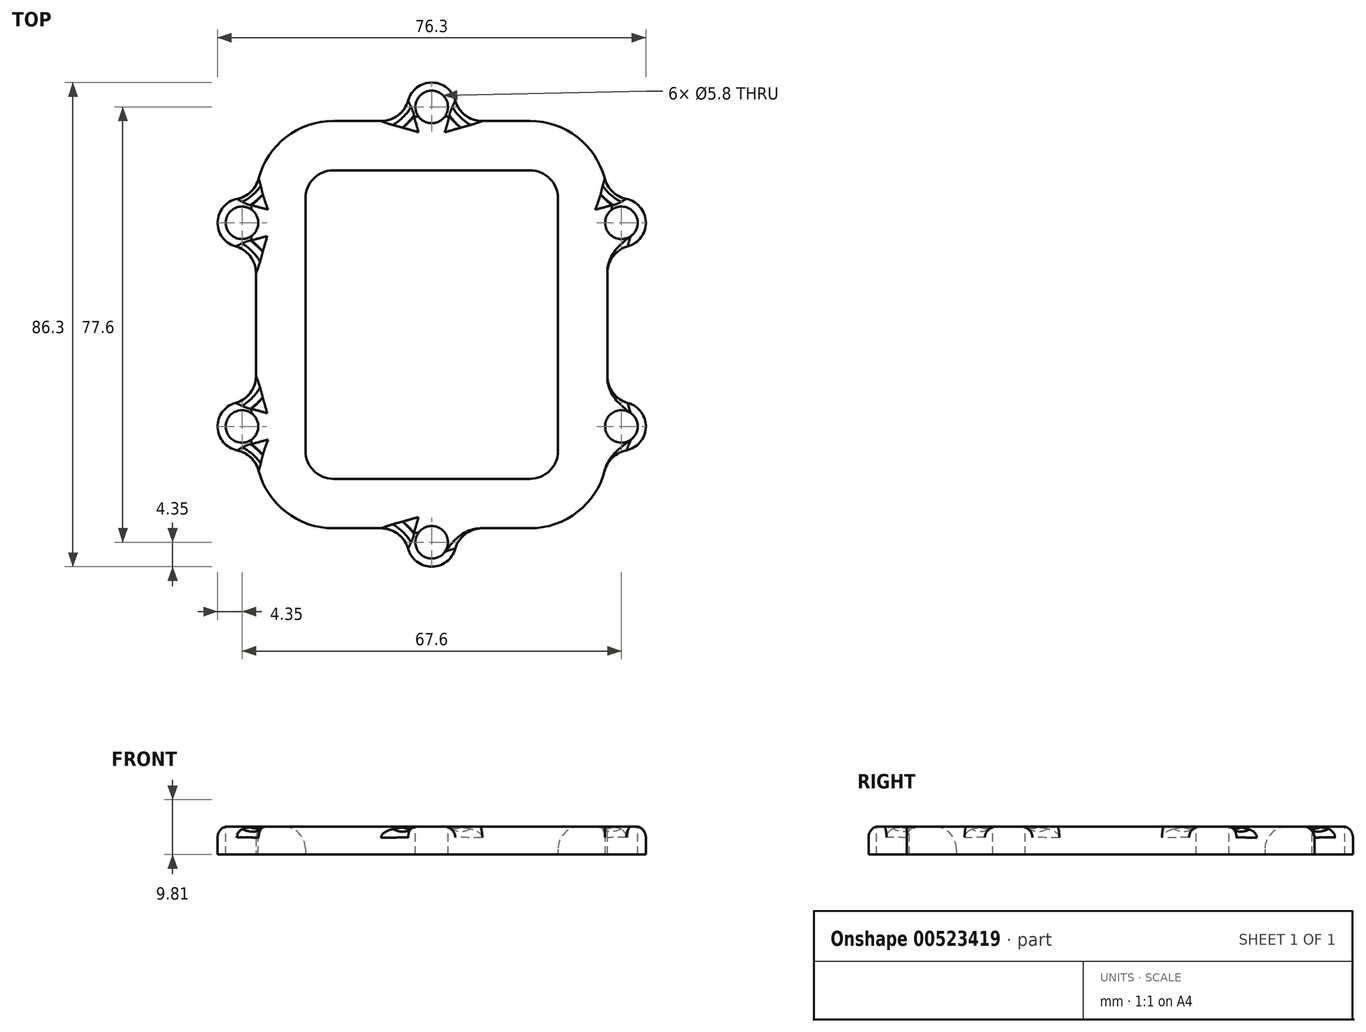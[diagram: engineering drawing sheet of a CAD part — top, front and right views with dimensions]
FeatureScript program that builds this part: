
annotation { "Feature Type Name" : "Feature", "Feature Type Description" : "" }
export const myFeature = defineFeature(function(context is Context, id is Id, definition is map)
    precondition{}
    {
        {
            var Q0;
            Q0=qCreatedBy(makeId("Top.planeOp"),FACE);
            var sketch = newSketch(context, id + "F0", { "sketchPlane" : qUnion([Q0])});
            skLineSegment(sketch, "E0.bottom", {"start": v(-17.5, -27.5) * mm, "end": v(17.5, -27.5) * mm});
            skLineSegment(sketch, "E0.top", {"start": v(-17.5, 27.5) * mm, "end": v(17.5, 27.5) * mm});
            skLineSegment(sketch, "E0.left", {"start": v(-22.5, -22.5) * mm, "end": v(-22.5, 22.5) * mm});
            skLineSegment(sketch, "E0.right", {"start": v(22.5, -22.5) * mm, "end": v(22.5, 22.5) * mm});
            skPoint(sketch, "E0.middle", {"position": v(0, 0) * mm});
            skPoint(sketch, "E1.visualSharp", {"position": v(22.5, -27.5) * mm});
            skArc(sketch, "E1.filletArc", {"start": v(17.5, -27.5) * mm, "mid": v(21.04, -26.04) * mm, "end": v(22.5, -22.5) * mm});
            skPoint(sketch, "E2.visualSharp", {"position": v(-22.5, -27.5) * mm});
            skArc(sketch, "E2.filletArc", {"start": v(-22.5, -22.5) * mm, "mid": v(-21.04, -26.04) * mm, "end": v(-17.5, -27.5) * mm});
            skPoint(sketch, "E3.visualSharp", {"position": v(-22.5, 27.5) * mm});
            skArc(sketch, "E3.filletArc", {"start": v(-17.5, 27.5) * mm, "mid": v(-21.04, 26.04) * mm, "end": v(-22.5, 22.5) * mm});
            skPoint(sketch, "E4.visualSharp", {"position": v(22.5, 27.5) * mm});
            skArc(sketch, "E4.filletArc", {"start": v(22.5, 22.5) * mm, "mid": v(21.04, 26.04) * mm, "end": v(17.5, 27.5) * mm});
            skArc(sketch, "E5.0", {"start": v(-31.3, -22.5) * mm, "mid": v(-27.26, -32.26) * mm, "end": v(-17.5, -36.3) * mm});
            skLineSegment(sketch, "E5.1", {"start": v(-17.5, -36.3) * mm, "end": v(0, -36.3) * mm});
            skLineSegment(sketch, "E5.2", {"start": v(-31.3, -22.5) * mm, "end": v(-31.3, 22.5) * mm});
            skArc(sketch, "E5.3", {"start": v(17.5, -36.3) * mm, "mid": v(27.26, -32.26) * mm, "end": v(31.3, -22.5) * mm});
            skArc(sketch, "E5.4", {"start": v(-17.5, 36.3) * mm, "mid": v(-27.26, 32.26) * mm, "end": v(-31.3, 22.5) * mm});
            skLineSegment(sketch, "E5.5", {"start": v(-17.5, 36.3) * mm, "end": v(0, 36.3) * mm});
            skArc(sketch, "E5.6", {"start": v(31.3, 22.5) * mm, "mid": v(27.26, 32.26) * mm, "end": v(17.5, 36.3) * mm});
            skLineSegment(sketch, "E5.7", {"start": v(31.3, -13.8) * mm, "end": v(31.3, 13.8) * mm});
            skCircle(sketch, "E6", {"center": v(-33.8, 18.15) * mm, "radius": 2.5 * mm, "construction": true});
            skLineSegment(sketch, "E7", {"start": v(-202.81, 0) * mm, "end": v(-26.87, 0) * mm, "construction": true});
            skCircle(sketch, "E8.MirrorC", {"center": v(33.8, 18.15) * mm, "radius": 2.5 * mm, "construction": true});
            skCircle(sketch, "E9.MirrorC", {"center": v(-33.8, -18.15) * mm, "radius": 2.5 * mm, "construction": true});
            skArc(sketch, "E10.MirrorCS", {"start": v(31.3, -22.5) * mm, "mid": v(27.26, -32.26) * mm, "end": v(17.5, -36.3) * mm});
            skLineSegment(sketch, "E11.MirrorCS", {"start": v(31.3, 13.8) * mm, "end": v(31.3, -13.8) * mm});
            skCircle(sketch, "E12.MirrorC", {"center": v(33.8, -18.15) * mm, "radius": 2.5 * mm, "construction": true});
            skPoint(sketch, "E13.orphan", {"position": v(31.3, 22.5) * mm});
            skCircle(sketch, "E14", {"center": v(0, 38.8) * mm, "radius": 2.5 * mm, "construction": true});
            skLineSegment(sketch, "E15.trimOffspring", {"start": v(0, 36.3) * mm, "end": v(17.5, 36.3) * mm});
            skCircle(sketch, "E16.MirrorC", {"center": v(0, -38.8) * mm, "radius": 2.5 * mm, "construction": true});
            skLineSegment(sketch, "E17.trimOffspring", {"start": v(0, -36.3) * mm, "end": v(17.5, -36.3) * mm});
            skLineSegment(sketch, "E18", {"start": v(0, 27.5) * mm, "end": v(0, 36.3) * mm, "construction": true});
            skLineSegment(sketch, "E19", {"start": v(-33.8, 0) * mm, "end": v(-33.8, 36.3) * mm, "construction": true});
            skArc(sketch, "E20.0", {"start": v(-25.5, -22.5) * mm, "mid": v(-23.16, -28.16) * mm, "end": v(-17.5, -30.5) * mm, "construction": true});
            skLineSegment(sketch, "E20.1", {"start": v(-17.5, -30.5) * mm, "end": v(17.5, -30.5) * mm, "construction": true});
            skLineSegment(sketch, "E20.2", {"start": v(-25.5, -22.5) * mm, "end": v(-25.5, 22.5) * mm, "construction": true});
            skArc(sketch, "E20.3", {"start": v(17.5, -30.5) * mm, "mid": v(23.16, -28.16) * mm, "end": v(25.5, -22.5) * mm, "construction": true});
            skArc(sketch, "E20.4", {"start": v(-17.5, 30.5) * mm, "mid": v(-23.16, 28.16) * mm, "end": v(-25.5, 22.5) * mm, "construction": true});
            skLineSegment(sketch, "E20.5", {"start": v(-17.5, 30.5) * mm, "end": v(17.5, 30.5) * mm, "construction": true});
            skArc(sketch, "E20.6", {"start": v(25.5, 22.5) * mm, "mid": v(23.16, 28.16) * mm, "end": v(17.5, 30.5) * mm, "construction": true});
            skLineSegment(sketch, "E20.7", {"start": v(25.5, -22.5) * mm, "end": v(25.5, 22.5) * mm, "construction": true});
            skArc(sketch, "E21.0", {"start": v(-28.3, -22.5) * mm, "mid": v(-25.14, -30.14) * mm, "end": v(-17.5, -33.3) * mm, "construction": true});
            skLineSegment(sketch, "E21.1", {"start": v(-17.5, -33.3) * mm, "end": v(17.5, -33.3) * mm, "construction": true});
            skLineSegment(sketch, "E21.2", {"start": v(-28.3, -22.5) * mm, "end": v(-28.3, 22.5) * mm, "construction": true});
            skArc(sketch, "E21.3", {"start": v(17.5, -33.3) * mm, "mid": v(25.14, -30.14) * mm, "end": v(28.3, -22.5) * mm, "construction": true});
            skArc(sketch, "E21.4", {"start": v(-17.5, 33.3) * mm, "mid": v(-25.14, 30.14) * mm, "end": v(-28.3, 22.5) * mm, "construction": true});
            skLineSegment(sketch, "E21.5", {"start": v(-17.5, 33.3) * mm, "end": v(17.5, 33.3) * mm, "construction": true});
            skArc(sketch, "E21.6", {"start": v(28.3, 22.5) * mm, "mid": v(25.14, 30.14) * mm, "end": v(17.5, 33.3) * mm, "construction": true});
            skLineSegment(sketch, "E21.7", {"start": v(28.3, -22.5) * mm, "end": v(28.3, 22.5) * mm, "construction": true});
            skArc(sketch, "E22", {"start": v(-33.8, 22.5) * mm, "mid": v(-38.15, 18.15) * mm, "end": v(-33.8, 13.8) * mm});
            skLineSegment(sketch, "E23", {"start": v(-33.8, 22.5) * mm, "end": v(-31.3, 22.5) * mm});
            skLineSegment(sketch, "E24", {"start": v(-33.8, 13.8) * mm, "end": v(-31.3, 13.8) * mm});
            skLineSegment(sketch, "E25", {"start": v(0, 27.5) * mm, "end": v(0, -27.5) * mm, "construction": true});
            skLineSegment(sketch, "E26.MirrorCS", {"start": v(33.8, 22.5) * mm, "end": v(31.3, 22.5) * mm});
            skArc(sketch, "E27.MirrorCS", {"start": v(33.8, 22.5) * mm, "mid": v(38.15, 18.15) * mm, "end": v(33.8, 13.8) * mm});
            skLineSegment(sketch, "E28.MirrorCS", {"start": v(33.8, 13.8) * mm, "end": v(31.3, 13.8) * mm});
            skArc(sketch, "E29.MirrorCS", {"start": v(-33.8, -22.5) * mm, "mid": v(-38.15, -18.15) * mm, "end": v(-33.8, -13.8) * mm});
            skLineSegment(sketch, "E30.MirrorCS", {"start": v(-33.8, -22.5) * mm, "end": v(-31.3, -22.5) * mm});
            skLineSegment(sketch, "E31.MirrorCS", {"start": v(33.8, -22.5) * mm, "end": v(31.3, -22.5) * mm});
            skArc(sketch, "E32.MirrorCS", {"start": v(33.8, -22.5) * mm, "mid": v(38.15, -18.15) * mm, "end": v(33.8, -13.8) * mm});
            skLineSegment(sketch, "E33.MirrorCS", {"start": v(33.8, -13.8) * mm, "end": v(31.3, -13.8) * mm});
            skLineSegment(sketch, "E34.MirrorCS", {"start": v(-33.8, -13.8) * mm, "end": v(-31.3, -13.8) * mm});
            skLineSegment(sketch, "E35", {"start": v(-4.35, 38.8) * mm, "end": v(-4.35, 36.3) * mm});
            skLineSegment(sketch, "E36", {"start": v(4.35, 38.8) * mm, "end": v(4.35, 36.3) * mm});
            skArc(sketch, "E37.trimOffspring", {"start": v(4.35, 38.8) * mm, "mid": v(0, 43.15) * mm, "end": v(-4.35, 38.8) * mm});
            skArc(sketch, "E38.MirrorCS", {"start": v(4.35, -38.8) * mm, "mid": v(0, -43.15) * mm, "end": v(-4.35, -38.8) * mm});
            skLineSegment(sketch, "E39.MirrorCS", {"start": v(-4.35, -38.8) * mm, "end": v(-4.35, -36.3) * mm});
            skLineSegment(sketch, "E40.MirrorCS", {"start": v(4.35, -38.8) * mm, "end": v(4.35, -36.3) * mm});
            skSolve(sketch);
        }
        {
            var Q0;
            Q0=qSketchRegion(id+"F0",true);
            extrude(context, id + "F1", {"entities" : qUnion([Q0]), "depth" : 5 * mm, "offsetDistance" : 25 * mm});
        }
        {
            var Q0;
            Q0=makeQuery(id+"F1.opExtrude","CAP_FACE",FACE,{"disambiguationData":[OSD([sQuery(id+"F0.wireOp",EDGE,"E0.bottom"),sQuery(id+"F0.wireOp",EDGE,"E0.top"),sQuery(id+"F0.wireOp",EDGE,"E0.left"),sQuery(id+"F0.wireOp",EDGE,"E0.right"),sQuery(id+"F0.wireOp",EDGE,"E1.filletArc"),sQuery(id+"F0.wireOp",EDGE,"E2.filletArc"),sQuery(id+"F0.wireOp",EDGE,"E3.filletArc"),sQuery(id+"F0.wireOp",EDGE,"E4.filletArc"),sQuery(id+"F0.wireOp",EDGE,"E5.0"),sQuery(id+"F0.wireOp",EDGE,"E5.1"),sQuery(id+"F0.wireOp",EDGE,"E5.2"),sQuery(id+"F0.wireOp",EDGE,"E5.4"),sQuery(id+"F0.wireOp",EDGE,"E5.5"),sQuery(id+"F0.wireOp",EDGE,"E5.6"),sQuery(id+"F0.wireOp",EDGE,"E10.MirrorCS"),sQuery(id+"F0.wireOp",EDGE,"E11.MirrorCS"),sQuery(id+"F0.wireOp",EDGE,"E15.trimOffspring"),sQuery(id+"F0.wireOp",EDGE,"E17.trimOffspring"),sQuery(id+"F0.wireOp",EDGE,"E22"),sQuery(id+"F0.wireOp",EDGE,"E23"),sQuery(id+"F0.wireOp",EDGE,"E24"),sQuery(id+"F0.wireOp",EDGE,"E26.MirrorCS"),sQuery(id+"F0.wireOp",EDGE,"E27.MirrorCS"),sQuery(id+"F0.wireOp",EDGE,"E28.MirrorCS"),sQuery(id+"F0.wireOp",EDGE,"E29.MirrorCS"),sQuery(id+"F0.wireOp",EDGE,"E30.MirrorCS"),sQuery(id+"F0.wireOp",EDGE,"E31.MirrorCS"),sQuery(id+"F0.wireOp",EDGE,"E32.MirrorCS"),sQuery(id+"F0.wireOp",EDGE,"E33.MirrorCS"),sQuery(id+"F0.wireOp",EDGE,"E34.MirrorCS"),sQuery(id+"F0.wireOp",EDGE,"E35"),sQuery(id+"F0.wireOp",EDGE,"E36"),sQuery(id+"F0.wireOp",EDGE,"E37.trimOffspring"),sQuery(id+"F0.wireOp",EDGE,"E38.MirrorCS"),sQuery(id+"F0.wireOp",EDGE,"E39.MirrorCS"),sQuery(id+"F0.wireOp",EDGE,"E40.MirrorCS")])],"isStart":false});
            var sketch = newSketch(context, id + "F2", { "sketchPlane" : qUnion([Q0])});
            skPoint(sketch, "E41", {"position": v(-33.8, 18.15) * mm});
            skPoint(sketch, "E42", {"position": v(0, 38.8) * mm});
            skPoint(sketch, "E43", {"position": v(33.8, 18.15) * mm});
            skPoint(sketch, "E44", {"position": v(33.8, -18.15) * mm});
            skPoint(sketch, "E45", {"position": v(0, -38.8) * mm});
            skPoint(sketch, "E46", {"position": v(-33.8, -18.15) * mm});
            skSolve(sketch);
        }
        {
            var Q0;
            Q0=sQuery(id+"F2.wireOp",VERTEX,"E41");
            var Q1;
            Q1=sQuery(id+"F2.wireOp",VERTEX,"E42");
            var Q2;
            Q2=sQuery(id+"F2.wireOp",VERTEX,"E43");
            var Q3;
            Q3=sQuery(id+"F2.wireOp",VERTEX,"E44");
            var Q4;
            Q4=sQuery(id+"F2.wireOp",VERTEX,"E45");
            var Q5;
            Q5=sQuery(id+"F2.wireOp",VERTEX,"E46");
            var Q6;
            Q6=makeQuery(id+"F1.opExtrude","SWEPT_BODY",BODY,{"disambiguationData":[OSD([sQuery(id+"F0.wireOp",EDGE,"E0.bottom"),sQuery(id+"F0.wireOp",EDGE,"E0.top"),sQuery(id+"F0.wireOp",EDGE,"E0.left"),sQuery(id+"F0.wireOp",EDGE,"E0.right"),sQuery(id+"F0.wireOp",EDGE,"E1.filletArc"),sQuery(id+"F0.wireOp",EDGE,"E2.filletArc"),sQuery(id+"F0.wireOp",EDGE,"E3.filletArc"),sQuery(id+"F0.wireOp",EDGE,"E4.filletArc"),sQuery(id+"F0.wireOp",EDGE,"E5.0"),sQuery(id+"F0.wireOp",EDGE,"E5.1"),sQuery(id+"F0.wireOp",EDGE,"E5.2"),sQuery(id+"F0.wireOp",EDGE,"E5.4"),sQuery(id+"F0.wireOp",EDGE,"E5.5"),sQuery(id+"F0.wireOp",EDGE,"E5.6"),sQuery(id+"F0.wireOp",EDGE,"E10.MirrorCS"),sQuery(id+"F0.wireOp",EDGE,"E11.MirrorCS"),sQuery(id+"F0.wireOp",EDGE,"E15.trimOffspring"),sQuery(id+"F0.wireOp",EDGE,"E17.trimOffspring"),sQuery(id+"F0.wireOp",EDGE,"E22"),sQuery(id+"F0.wireOp",EDGE,"E23"),sQuery(id+"F0.wireOp",EDGE,"E24"),sQuery(id+"F0.wireOp",EDGE,"E26.MirrorCS"),sQuery(id+"F0.wireOp",EDGE,"E27.MirrorCS"),sQuery(id+"F0.wireOp",EDGE,"E28.MirrorCS"),sQuery(id+"F0.wireOp",EDGE,"E29.MirrorCS"),sQuery(id+"F0.wireOp",EDGE,"E30.MirrorCS"),sQuery(id+"F0.wireOp",EDGE,"E31.MirrorCS"),sQuery(id+"F0.wireOp",EDGE,"E32.MirrorCS"),sQuery(id+"F0.wireOp",EDGE,"E33.MirrorCS"),sQuery(id+"F0.wireOp",EDGE,"E34.MirrorCS"),sQuery(id+"F0.wireOp",EDGE,"E35"),sQuery(id+"F0.wireOp",EDGE,"E36"),sQuery(id+"F0.wireOp",EDGE,"E37.trimOffspring"),sQuery(id+"F0.wireOp",EDGE,"E38.MirrorCS"),sQuery(id+"F0.wireOp",EDGE,"E39.MirrorCS"),sQuery(id+"F0.wireOp",EDGE,"E40.MirrorCS")])]});
            hole(context, id + "F3", {"style" : HoleStyle.SIMPLE, "endStyle" : HoleEndStyle.THROUGH, "standardTappedOrClearance" : lookupTablePath({ "fit" : "Loose", "standard" : "ISO", "size" : "M5", "type" : "Clearance" }), "standardBlindInLast" : lookupTablePath({ "fit" : "Loose", "standard" : "ISO", "engagement" : "75%", "pitch" : "0.8 mm", "size" : "M5", "type" : "Clearance & tapped" }), "holeDiameter" : 5.8 * mm, "majorDiameter" : 5 * mm, "isTappedThrough" : true, "tappedDepth" : 37.6 * mm, "tapClearance" : 3, "locations" : qUnion([Q0, Q1, Q2, Q3, Q4, Q5]), "scope" : qUnion([Q6])});
        }
        {
            var Q0;
            Q0=makeQuery(id+"F1.opExtrude","CAP_EDGE",EDGE,{"disambiguationData":[OSD([sQuery(id+"F0.wireOp",EDGE,"E0.top")])],"isStart":false});
            fillet(context, id + "F4", {"entities" : qUnion([Q0]), "radius" : 4 * mm, "tangentPropagation" : true, "defaultsChanged" : true, "vertexSettings" : [], "allowEdgeOverflow" : false});
        }
        {
            var Q0;
            Q0=makeQuery(id+"F1.opExtrude","CAP_EDGE",EDGE,{"disambiguationData":[OSD([sQuery(id+"F0.wireOp",EDGE,"E22")])],"isStart":false});
            var Q1;
            Q1=makeQuery(id+"F1.opExtrude","CAP_EDGE",EDGE,{"disambiguationData":[OSD([sQuery(id+"F0.wireOp",EDGE,"E5.4")])],"isStart":false});
            var Q2;
            Q2=makeQuery(id+"F1.opExtrude","CAP_EDGE",EDGE,{"disambiguationData":[OSD([sQuery(id+"F0.wireOp",EDGE,"E37.trimOffspring")])],"isStart":false});
            var Q3;
            Q3=makeQuery(id+"F1.opExtrude","CAP_EDGE",EDGE,{"disambiguationData":[OSD([sQuery(id+"F0.wireOp",EDGE,"E5.2")])],"isStart":false});
            var Q4;
            Q4=makeQuery(id+"F1.opExtrude","CAP_EDGE",EDGE,{"disambiguationData":[OSD([sQuery(id+"F0.wireOp",EDGE,"E29.MirrorCS")])],"isStart":false});
            var Q5;
            Q5=makeQuery(id+"F1.opExtrude","CAP_EDGE",EDGE,{"disambiguationData":[OSD([sQuery(id+"F0.wireOp",EDGE,"E39.MirrorCS")])],"isStart":false});
            var Q6;
            Q6=makeQuery(id+"F1.opExtrude","CAP_EDGE",EDGE,{"disambiguationData":[OSD([sQuery(id+"F0.wireOp",EDGE,"E5.1")])],"isStart":false});
            var Q7;
            Q7=makeQuery(id+"F1.opExtrude","CAP_EDGE",EDGE,{"disambiguationData":[OSD([sQuery(id+"F0.wireOp",EDGE,"E10.MirrorCS")])],"isStart":false});
            var Q8;
            Q8=makeQuery(id+"F1.opExtrude","CAP_EDGE",EDGE,{"disambiguationData":[OSD([sQuery(id+"F0.wireOp",EDGE,"E31.MirrorCS")])],"isStart":false});
            var Q9;
            Q9=makeQuery(id+"F1.opExtrude","CAP_EDGE",EDGE,{"disambiguationData":[OSD([sQuery(id+"F0.wireOp",EDGE,"E33.MirrorCS")])],"isStart":false});
            var Q10;
            Q10=makeQuery(id+"F1.opExtrude","CAP_EDGE",EDGE,{"disambiguationData":[OSD([sQuery(id+"F0.wireOp",EDGE,"E28.MirrorCS")])],"isStart":false});
            var Q11;
            Q11=makeQuery(id+"F1.opExtrude","CAP_EDGE",EDGE,{"disambiguationData":[OSD([sQuery(id+"F0.wireOp",EDGE,"E5.6")])],"isStart":false});
            fillet(context, id + "F5", {"entities" : qUnion([Q0, Q1, Q2, Q3, Q4, Q5, Q6, Q7, Q8, Q9, Q10, Q11]), "tangentPropagation" : true, "radius" : 2 * mm, "defaultsChanged" : false, "vertexSettings" : [], "allowEdgeOverflow" : false});
        }
        {
            var Q0;
            Q0=makeQuery(id+"F1.opExtrude","SWEPT_EDGE",EDGE,{"disambiguationData":[OSD([sQuery(id+"F0.wireOp",EDGE,"E11.MirrorCS"),sQuery(id+"F0.wireOp",EDGE,"E33.MirrorCS")])]});
            var Q1;
            Q1=makeQuery(id+"F1.opExtrude","SWEPT_EDGE",EDGE,{"disambiguationData":[OSD([sQuery(id+"F0.wireOp",EDGE,"E11.MirrorCS"),sQuery(id+"F0.wireOp",EDGE,"E28.MirrorCS")])]});
            var Q2;
            Q2=makeQuery(id+"F1.opExtrude","SWEPT_EDGE",EDGE,{"disambiguationData":[OSD([sQuery(id+"F0.wireOp",EDGE,"E10.MirrorCS"),sQuery(id+"F0.wireOp",EDGE,"E31.MirrorCS")])]});
            var Q3;
            Q3=makeQuery(id+"F1.opExtrude","SWEPT_EDGE",EDGE,{"disambiguationData":[OSD([sQuery(id+"F0.wireOp",EDGE,"E17.trimOffspring"),sQuery(id+"F0.wireOp",EDGE,"E40.MirrorCS")])]});
            var Q4;
            Q4=makeQuery(id+"F1.opExtrude","SWEPT_EDGE",EDGE,{"disambiguationData":[OSD([sQuery(id+"F0.wireOp",EDGE,"E5.1"),sQuery(id+"F0.wireOp",EDGE,"E39.MirrorCS")])]});
            var Q5;
            Q5=makeQuery(id+"F1.opExtrude","SWEPT_EDGE",EDGE,{"disambiguationData":[OSD([sQuery(id+"F0.wireOp",EDGE,"E5.0"),sQuery(id+"F0.wireOp",EDGE,"E5.2"),sQuery(id+"F0.wireOp",EDGE,"E30.MirrorCS")])]});
            var Q6;
            Q6=makeQuery(id+"F1.opExtrude","SWEPT_EDGE",EDGE,{"disambiguationData":[OSD([sQuery(id+"F0.wireOp",EDGE,"E5.2"),sQuery(id+"F0.wireOp",EDGE,"E24")])]});
            var Q7;
            Q7=makeQuery(id+"F1.opExtrude","SWEPT_EDGE",EDGE,{"disambiguationData":[OSD([sQuery(id+"F0.wireOp",EDGE,"E5.2"),sQuery(id+"F0.wireOp",EDGE,"E34.MirrorCS")])]});
            var Q8;
            Q8=makeQuery(id+"F1.opExtrude","SWEPT_EDGE",EDGE,{"disambiguationData":[OSD([sQuery(id+"F0.wireOp",EDGE,"E5.2"),sQuery(id+"F0.wireOp",EDGE,"E5.4"),sQuery(id+"F0.wireOp",EDGE,"E23")])]});
            var Q9;
            Q9=makeQuery(id+"F1.opExtrude","SWEPT_EDGE",EDGE,{"disambiguationData":[OSD([sQuery(id+"F0.wireOp",EDGE,"E5.5"),sQuery(id+"F0.wireOp",EDGE,"E35")])]});
            var Q10;
            Q10=makeQuery(id+"F1.opExtrude","SWEPT_EDGE",EDGE,{"disambiguationData":[OSD([sQuery(id+"F0.wireOp",EDGE,"E5.6"),sQuery(id+"F0.wireOp",EDGE,"E26.MirrorCS")])]});
            var Q11;
            Q11=makeQuery(id+"F1.opExtrude","SWEPT_EDGE",EDGE,{"disambiguationData":[OSD([sQuery(id+"F0.wireOp",EDGE,"E15.trimOffspring"),sQuery(id+"F0.wireOp",EDGE,"E36")])]});
            fillet(context, id + "F6", {"entities" : qUnion([Q0, Q1, Q2, Q3, Q4, Q5, Q6, Q7, Q8, Q9, Q10, Q11]), "tangentPropagation" : true, "radius" : 5 * mm, "defaultsChanged" : false, "vertexSettings" : [], "allowEdgeOverflow" : false});
        }
    });
